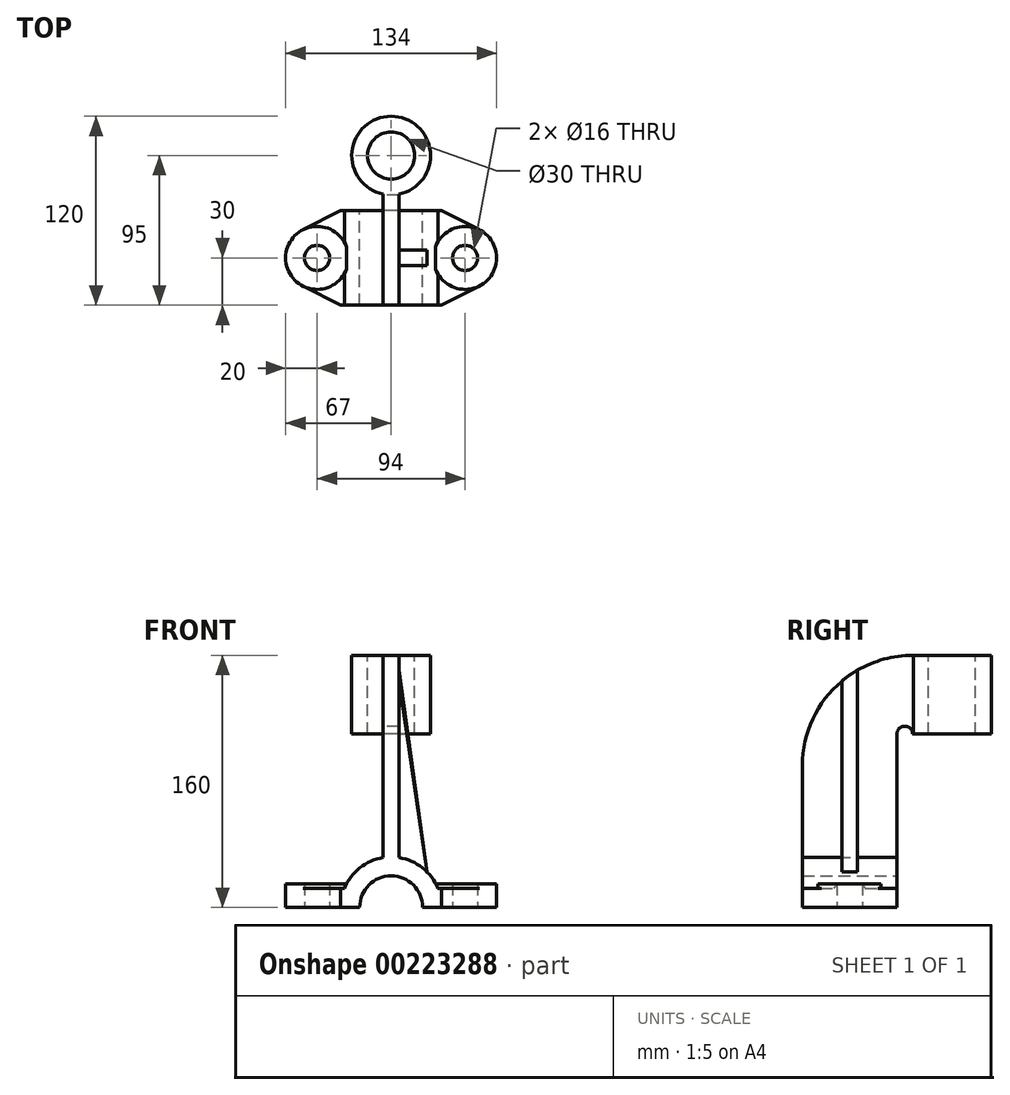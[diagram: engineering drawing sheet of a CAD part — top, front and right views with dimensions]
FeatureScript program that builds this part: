
annotation { "Feature Type Name" : "Feature", "Feature Type Description" : "" }
export const myFeature = defineFeature(function(context is Context, id is Id, definition is map)
    precondition{}
    {
        {
            var Q0;
            Q0=qCreatedBy(makeId("Front.planeOp"),FACE);
            var sketch = newSketch(context, id + "F0", { "sketchPlane" : qUnion([Q0])});
            skCircle(sketch, "E0", {"center": v(0, 0) * mm, "radius": 20 * mm});
            skCircle(sketch, "E1", {"center": v(0, 0) * mm, "radius": 32 * mm});
            skLineSegment(sketch, "E2", {"start": v(-32, 0) * mm, "end": v(-20, 0) * mm});
            skPoint(sketch, "E3.orphan", {"position": v(-73.06, 0) * mm});
            skLineSegment(sketch, "E4.trimOffspring", {"start": v(20, 0) * mm, "end": v(32, 0) * mm});
            skSolve(sketch);
        }
        {
            var Q0;
            {var subQ0=sQuery(id+"F0.wireOp",EDGE,"E2");Q0=makeQuery(id+"F0.imprint","IMPRINT",FACE,{"disambiguationData":[TD([[makeQuery(id+"F0.imprint","IMPRINT",EDGE,{"derivedFrom":subQ0}),1.0]])]});}
            extrude(context, id + "F1", {"entities" : qUnion([Q0]), "endBound" : BoundingType.SYMMETRIC, "depth" : 60 * mm});
        }
        {
            var Q0;
            Q0=qCreatedBy(makeId("Top.planeOp"),FACE);
            var sketch = newSketch(context, id + "F2", { "sketchPlane" : qUnion([Q0])});
            skPoint(sketch, "E5.0", {"position": v(-32, 30) * mm});
            skPoint(sketch, "E6.0", {"position": v(-32, -30) * mm});
            skArc(sketch, "E7", {"start": v(-32, 13.23) * mm, "mid": v(-67, 0) * mm, "end": v(-32, -13.23) * mm});
            skCircle(sketch, "E8", {"center": v(-47, 0) * mm, "radius": 8 * mm});
            skLineSegment(sketch, "E9", {"start": v(-32, 30) * mm, "end": v(-56.03, 17.85) * mm});
            skLineSegment(sketch, "E10", {"start": v(-32, -30) * mm, "end": v(-56.03, -17.85) * mm});
            skLineSegment(sketch, "E11", {"start": v(-32, 30) * mm, "end": v(-22, 30) * mm});
            skLineSegment(sketch, "E12", {"start": v(-22, 30) * mm, "end": v(-22, 13.37) * mm});
            skLineSegment(sketch, "E13", {"start": v(-16.72, 0) * mm, "end": v(-74.86, 0) * mm, "construction": true});
            skLineSegment(sketch, "E14.MirrorCS", {"start": v(-22, -30) * mm, "end": v(-22, -13.37) * mm});
            skLineSegment(sketch, "E15.MirrorCS", {"start": v(-32, -30) * mm, "end": v(-22, -30) * mm});
            skPoint(sketch, "E16.MirrorCS.start.orphan", {"position": v(-22, -13.37) * mm});
            skLineSegment(sketch, "E17", {"start": v(-22, 13.37) * mm, "end": v(-22, -13.37) * mm});
            skCircle(sketch, "E18", {"center": v(-47, 0) * mm, "radius": 20 * mm});
            skSolve(sketch);
        }
        {
            var Q0;
            Q0=makeQuery(id+"F2.imprint","IMPRINT",FACE,{"disambiguationData":[TD([[makeQuery(id+"F2.imprint","IMPRINT",EDGE,{"derivedFrom":sQuery(id+"F2.wireOp",EDGE,"E8")}),-1.0]])]});
            extrude(context, id + "F3", {"entities" : qUnion([Q0]), "operationType" : NewBodyOperationType.ADD, "depth" : 15 * mm});
        }
        {
            var Q0;
            {var subQ0=sQuery(id+"F2.wireOp",EDGE,"E9");Q0=makeQuery(id+"F2.imprint","IMPRINT",FACE,{"disambiguationData":[TD([[makeQuery(id+"F2.imprint","IMPRINT",EDGE,{"derivedFrom":subQ0}),1.0]])]});}
            var Q1;
            {var subQ0=sQuery(id+"F2.wireOp",EDGE,"E10");Q1=makeQuery(id+"F2.imprint","IMPRINT",FACE,{"disambiguationData":[TD([[makeQuery(id+"F2.imprint","IMPRINT",EDGE,{"derivedFrom":subQ0}),-1.0]])]});}
            extrude(context, id + "F4", {"entities" : qUnion([Q0, Q1]), "operationType" : NewBodyOperationType.ADD, "depth" : 12 * mm});
        }
        {
            var Q0;
            Q0=makeQuery(id+"F1.opExtrude","SWEPT_BODY",BODY,{"disambiguationData":[OSD([sQuery(id+"F0.wireOp",EDGE,"E0"),sQuery(id+"F0.wireOp",EDGE,"E1"),sQuery(id+"F0.wireOp",EDGE,"E2"),sQuery(id+"F0.wireOp",EDGE,"E4.trimOffspring")])]});
            var Q1;
            Q1=qCreatedBy(makeId("Right.planeOp"),FACE);
            mirror(context, id + "F5", {"operationType" : NewBodyOperationType.ADD, "entities" : qUnion([Q0]), "mirrorPlane" : qUnion([Q1])});
        }
        {
            var Q0;
            Q0=qCreatedBy(makeId("Top.planeOp"),FACE);
            cPlane(context, id + "F6", {"entities" : qUnion([Q0]), "cplaneType" : CPlaneType.OFFSET, "offset" : 160 * mm, "width" : 150 * mm, "height" : 150 * mm});
        }
        {
            var Q0;
            Q0=qCreatedBy(id+"F6.planeOp",FACE);
            var sketch = newSketch(context, id + "F7", { "sketchPlane" : qUnion([Q0])});
            skCircle(sketch, "E19", {"center": v(0, 65) * mm, "radius": 25 * mm});
            skCircle(sketch, "E20", {"center": v(0, 65) * mm, "radius": 15 * mm});
            skLineSegment(sketch, "E21.0", {"start": v(29.66, -30) * mm, "end": v(-29.66, -30) * mm, "construction": true});
            skSolve(sketch);
        }
        {
            var Q0;
            Q0=makeQuery(id+"F7.imprint","IMPRINT",FACE,{"disambiguationData":[TD([[makeQuery(id+"F7.imprint","IMPRINT",EDGE,{"derivedFrom":sQuery(id+"F7.wireOp",EDGE,"E19")}),1.0]])]});
            extrude(context, id + "F8", {"entities" : qUnion([Q0]), "oppositeDirection" : true, "depth" : 50 * mm});
        }
        {
            var Q0;
            Q0=qCreatedBy(makeId("Right.planeOp"),FACE);
            var sketch = newSketch(context, id + "F9", { "sketchPlane" : qUnion([Q0])});
            skPoint(sketch, "E22.0", {"position": v(-30, 32) * mm});
            skPoint(sketch, "E23.0", {"position": v(30, 32) * mm});
            skLineSegment(sketch, "E24", {"start": v(40, 110) * mm, "end": v(40, 160) * mm, "construction": true});
            skLineSegment(sketch, "E25", {"start": v(-30, 32) * mm, "end": v(-30, 90) * mm});
            skArc(sketch, "E26", {"start": v(40, 160) * mm, "mid": v(-9.5, 139.5) * mm, "end": v(-30, 90) * mm});
            skLineSegment(sketch, "E27", {"start": v(30, 32) * mm, "end": v(30, 110) * mm});
            skArc(sketch, "E28", {"start": v(40, 110) * mm, "mid": v(35, 115) * mm, "end": v(30, 110) * mm});
            skPoint(sketch, "E29.0", {"position": v(-30, 20) * mm});
            skPoint(sketch, "E30.0", {"position": v(30, 20) * mm});
            skLineSegment(sketch, "E31", {"start": v(-30, 32) * mm, "end": v(-30, 20) * mm});
            skLineSegment(sketch, "E32", {"start": v(30, 20) * mm, "end": v(30, 32) * mm});
            skLineSegment(sketch, "E33", {"start": v(30, 20) * mm, "end": v(-30, 20) * mm});
            skLineSegment(sketch, "E34", {"start": v(40, 160) * mm, "end": v(50, 160) * mm});
            skLineSegment(sketch, "E35", {"start": v(50, 160) * mm, "end": v(50, 110) * mm});
            skLineSegment(sketch, "E36", {"start": v(50, 110) * mm, "end": v(40, 110) * mm});
            skSolve(sketch);
        }
        {
            var Q0;
            Q0=makeQuery(id+"F9.imprint","IMPRINT",FACE,{"disambiguationData":[TD([[makeQuery(id+"F9.imprint","IMPRINT",EDGE,{"derivedFrom":sQuery(id+"F9.wireOp",EDGE,"E25")}),-1.0]])]});
            extrude(context, id + "F10", {"entities" : qUnion([Q0]), "operationType" : NewBodyOperationType.ADD, "endBound" : BoundingType.SYMMETRIC, "depth" : 10 * mm});
        }
        {
            var Q0;
            {var subQ0=makeQuery(id+"F4.boolean.opBoolean","MERGE",FACE,{"derivedFrom":[makeQuery(id+"F1.opExtrude","CAP_FACE",FACE,{"disambiguationData":[OSD([sQuery(id+"F0.wireOp",EDGE,"E0"),sQuery(id+"F0.wireOp",EDGE,"E1"),sQuery(id+"F0.wireOp",EDGE,"E2"),sQuery(id+"F0.wireOp",EDGE,"E4.trimOffspring")])],"isStart":false}),makeQuery(id+"F4.opExtrude","SWEPT_FACE",FACE,{"disambiguationData":[OSD([sQuery(id+"F2.wireOp",EDGE,"E15.MirrorCS")])]})]});Q0=makeQuery(id+"F10.boolean.opBoolean","MERGE",FACE,{"derivedFrom":[makeQuery(id+"F5.boolean.opBoolean","MERGE",FACE,{"derivedFrom":[subQ0,makeQuery(id+"F5.opPattern","COPY",FACE,{"derivedFrom":subQ0,"instanceName":"1"})]}),makeQuery(id+"F10.opExtrude","SWEPT_FACE",FACE,{"disambiguationData":[OSD([sQuery(id+"F9.wireOp",EDGE,"E25"),sQuery(id+"F9.wireOp",EDGE,"E31")])]})]});}
            cPlane(context, id + "F11", {"entities" : qUnion([Q0]), "cplaneType" : CPlaneType.OFFSET, "offset" : 35 * mm, "oppositeDirection" : true, "width" : 150 * mm, "height" : 150 * mm});
        }
        {
            var Q0;
            {var subQ0=makeQuery(id+"F4.boolean.opBoolean","MERGE",FACE,{"derivedFrom":[makeQuery(id+"F1.opExtrude","CAP_FACE",FACE,{"disambiguationData":[OSD([sQuery(id+"F0.wireOp",EDGE,"E0"),sQuery(id+"F0.wireOp",EDGE,"E1"),sQuery(id+"F0.wireOp",EDGE,"E2"),sQuery(id+"F0.wireOp",EDGE,"E4.trimOffspring")])],"isStart":false}),makeQuery(id+"F4.opExtrude","SWEPT_FACE",FACE,{"disambiguationData":[OSD([sQuery(id+"F2.wireOp",EDGE,"E15.MirrorCS")])]})]});Q0=makeQuery(id+"F10.boolean.opBoolean","MERGE",FACE,{"derivedFrom":[makeQuery(id+"F5.boolean.opBoolean","MERGE",FACE,{"derivedFrom":[subQ0,makeQuery(id+"F5.opPattern","COPY",FACE,{"derivedFrom":subQ0,"instanceName":"1"})]}),makeQuery(id+"F10.opExtrude","SWEPT_FACE",FACE,{"disambiguationData":[OSD([sQuery(id+"F9.wireOp",EDGE,"E25"),sQuery(id+"F9.wireOp",EDGE,"E31")])]})]});}
            cPlane(context, id + "F12", {"entities" : qUnion([Q0]), "cplaneType" : CPlaneType.OFFSET, "offset" : 30 * mm, "oppositeDirection" : true, "width" : 150 * mm, "height" : 150 * mm});
        }
        {
            var Q0;
            {var subQ0=makeQuery(id+"F4.boolean.opBoolean","MERGE",FACE,{"derivedFrom":[makeQuery(id+"F1.opExtrude","CAP_FACE",FACE,{"disambiguationData":[OSD([sQuery(id+"F0.wireOp",EDGE,"E0"),sQuery(id+"F0.wireOp",EDGE,"E1"),sQuery(id+"F0.wireOp",EDGE,"E2"),sQuery(id+"F0.wireOp",EDGE,"E4.trimOffspring")])],"isStart":false}),makeQuery(id+"F4.opExtrude","SWEPT_FACE",FACE,{"disambiguationData":[OSD([sQuery(id+"F2.wireOp",EDGE,"E15.MirrorCS")])]})]});Q0=makeQuery(id+"F10.boolean.opBoolean","MERGE",FACE,{"derivedFrom":[makeQuery(id+"F5.boolean.opBoolean","MERGE",FACE,{"derivedFrom":[subQ0,makeQuery(id+"F5.opPattern","COPY",FACE,{"derivedFrom":subQ0,"instanceName":"1"})]}),makeQuery(id+"F10.opExtrude","SWEPT_FACE",FACE,{"disambiguationData":[OSD([sQuery(id+"F9.wireOp",EDGE,"E25"),sQuery(id+"F9.wireOp",EDGE,"E31")])]})]});}
            cPlane(context, id + "F13", {"entities" : qUnion([Q0]), "cplaneType" : CPlaneType.OFFSET, "offset" : 25 * mm, "oppositeDirection" : true, "width" : 150 * mm, "height" : 150 * mm});
        }
        {
            var Q0;
            Q0=qCreatedBy(id+"F11.planeOp",FACE);
            var sketch = newSketch(context, id + "F14", { "sketchPlane" : qUnion([Q0])});
            skLineSegment(sketch, "E37", {"start": v(5, 31.6) * mm, "end": v(5, 150.62) * mm});
            skArc(sketch, "E38", {"start": v(5, 31.6) * mm, "mid": v(14.63, 28.46) * mm, "end": v(22.79, 22.47) * mm});
            skPoint(sketch, "E39", {"position": v(22.79, 22.47) * mm});
            skLineSegment(sketch, "E40", {"start": v(22.79, 22.47) * mm, "end": v(5, 150.62) * mm});
            skPoint(sketch, "E41.orphan", {"position": v(28.27, 15) * mm});
            skSolve(sketch);
        }
        {
            var Q0;
            Q0=qCreatedBy(id+"F12.planeOp",FACE);
            var sketch = newSketch(context, id + "F15", { "sketchPlane" : qUnion([Q0])});
            skLineSegment(sketch, "E42", {"start": v(5, 31.6) * mm, "end": v(5, 147.45) * mm});
            skArc(sketch, "E43", {"start": v(5, 31.6) * mm, "mid": v(14.63, 28.46) * mm, "end": v(22.79, 22.47) * mm});
            skPoint(sketch, "E44.0", {"position": v(22.79, 22.47) * mm});
            skLineSegment(sketch, "E45", {"start": v(5, 147.45) * mm, "end": v(22.79, 22.47) * mm});
            skPoint(sketch, "E46.orphan", {"position": v(28.27, 15) * mm});
            skSolve(sketch);
        }
        {
            var Q0;
            Q0=qCreatedBy(id+"F13.planeOp",FACE);
            var sketch = newSketch(context, id + "F16", { "sketchPlane" : qUnion([Q0])});
            skLineSegment(sketch, "E47", {"start": v(5, 31.6) * mm, "end": v(5, 143.62) * mm});
            skArc(sketch, "E48", {"start": v(5, 31.6) * mm, "mid": v(14.63, 28.46) * mm, "end": v(22.79, 22.47) * mm});
            skPoint(sketch, "E49.0", {"position": v(22.79, 22.47) * mm});
            skLineSegment(sketch, "E50", {"start": v(5, 143.62) * mm, "end": v(22.79, 22.47) * mm});
            skPoint(sketch, "E51.orphan", {"position": v(28.27, 15) * mm});
            skSolve(sketch);
        }
        {
            var Q1;
            Q1 = qSketchRegion(id + "F14", true);
            var Q2;
            Q2 = qSketchRegion(id + "F15", true);
            var Q3;
            Q3 = qSketchRegion(id + "F16", true);
            loft(context, id + "F17", {"operationType" : NewBodyOperationType.ADD, "sheetProfilesArray" : [{ "sheetProfileEntities" : qUnion([Q1]) }, { "sheetProfileEntities" : qUnion([Q2]) }, { "sheetProfileEntities" : qUnion([Q3]) }]});
        }
    });
